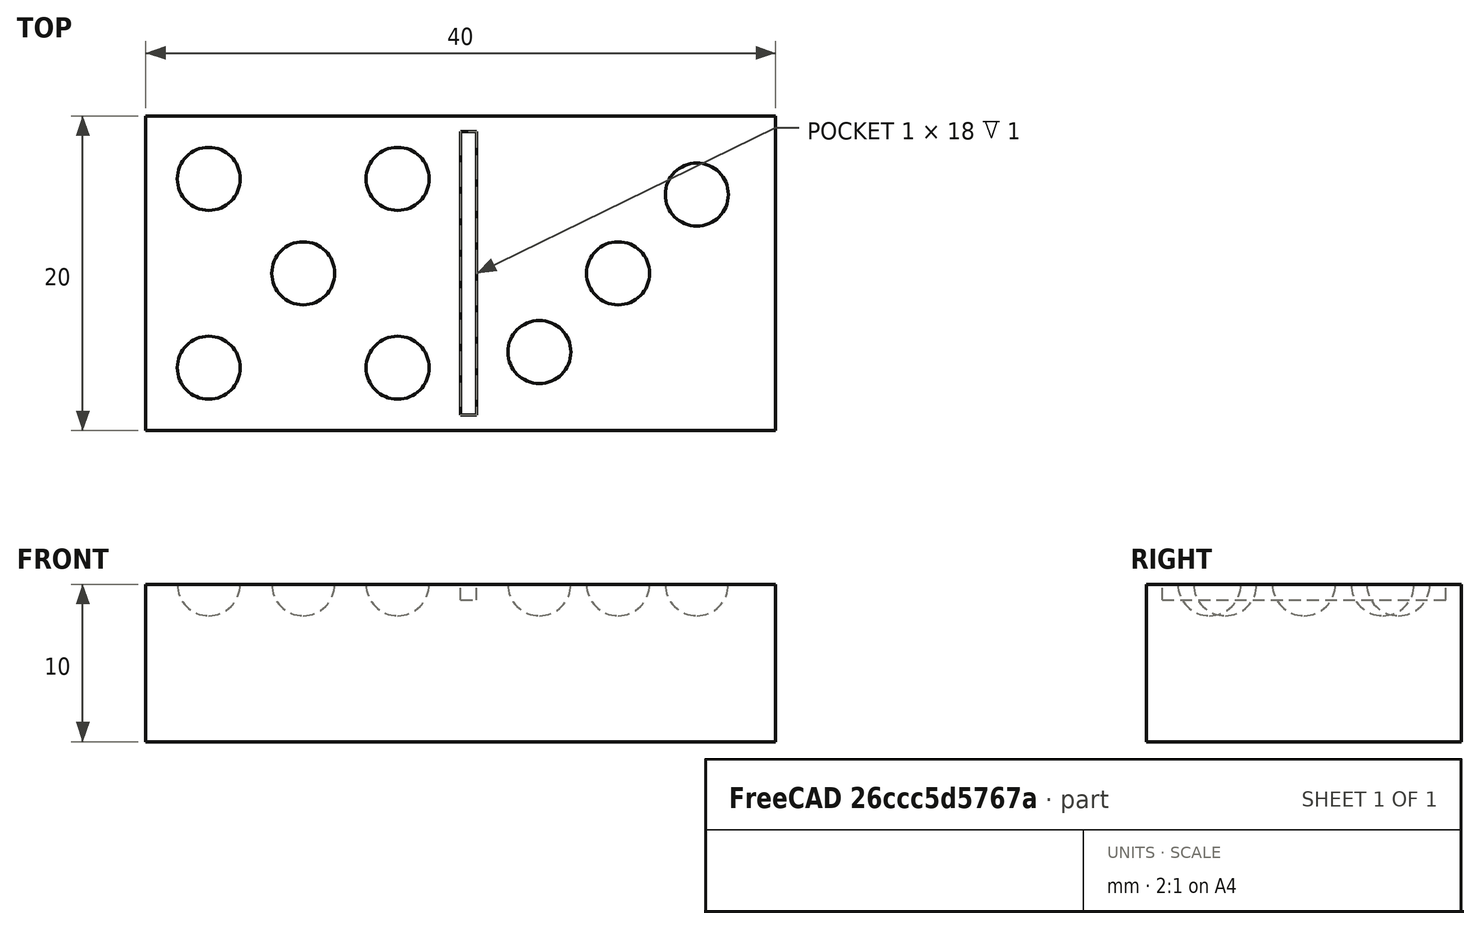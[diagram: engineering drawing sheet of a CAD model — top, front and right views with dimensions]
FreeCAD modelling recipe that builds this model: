
FCSTD DOCUMENT  (FreeCAD 0.16R6707 (Git))
Label: Ficha_Domino
License: CreativeCommons Attribution-ShareAlike
LicenseURL: http://creativecommons.org/licenses/by-sa/4.0/
objects: Part::Cut×3, Part::Sphere×3, Part::Box×2, Part::FeaturePython×2, Part::MultiFuse×1
note: 11 computed .brp shape members not serialized (recipe doc carries the construction recipe); baked Part::Feature solids carry a one-line shape summary decoded from their .brp

FEATURE [Part::Box] Box  label="Base"
  Height = 10
  Length = 40
  Width = 20
FEATURE [Part::Box] Box001  label="Separador"
  Height = 1
  Length = 1
  Placement = pos=(20,1,9) rot=(0,0,1;0rad)
  Width = 18
FEATURE [Part::Cut] Cut  label="Base_cortada"
  Base = -> Box
  Tool = -> Box001
FEATURE [Part::Sphere] Sphere
  Angle1 = -90
  Angle2 = 90
  Angle3 = 360
  Radius = 2
FEATURE [Part::FeaturePython] Array  label="numero3"  # Draft array (typed FeaturePython)
  Angle = 360
  ArrayType = 0
  Axis = (0,0,1)
  Base = -> Sphere
  Center = (0,0,0)
  Fuse = false
  IntervalAxis = (0,0,0)
  IntervalX = (5,5,0)
  IntervalY = (0,1,0)
  IntervalZ = (0,0,0)
  NumberPolar = 1
  NumberX = 3
  NumberY = 1
  NumberZ = 1
  Placement = pos=(25,5,10) rot=(0,0,1;0rad)
FEATURE [Part::Cut] Cut001  label="Solo3"
  Base = -> Cut
  Tool = -> Array
FEATURE [Part::Sphere] Sphere001
  Angle1 = -90
  Angle2 = 90
  Angle3 = 360
  Placement = pos=(10,10,10) rot=(0,0,1;0rad)
  Radius = 2
FEATURE [Part::Sphere] Sphere002
  Angle1 = -90
  Angle2 = 90
  Angle3 = 360
  Placement = pos=(4,4,10) rot=(0,0,1;0rad)
  Radius = 2
FEATURE [Part::FeaturePython] Array001  # Draft array (typed FeaturePython)
  Angle = 360
  ArrayType = 0
  Axis = (0,0,1)
  Base = -> Sphere002
  Center = (0,0,0)
  Fuse = false
  IntervalAxis = (0,0,0)
  IntervalX = (12,0,0)
  IntervalY = (0,12,0)
  IntervalZ = (0,0,0)
  NumberPolar = 1
  NumberX = 2
  NumberY = 2
  NumberZ = 1
FEATURE [Part::MultiFuse] Fusion  label="Numero5"
  Shapes = -> [Sphere001,Array001]
FEATURE [Part::Cut] Cut002  label="Ficha"
  Base = -> Cut001
  Tool = -> Fusion
